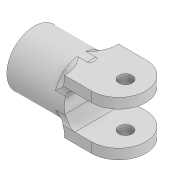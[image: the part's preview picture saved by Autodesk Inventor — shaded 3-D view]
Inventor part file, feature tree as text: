
AUTODESK INVENTOR PART (.ipt)
format: ipt  version: 2022 (Build 260153000, 153)  size: 236,544 bytes
history: native  units: mm
features: extrude x4, sketch x4, fillet x3, projected_geometry x1
ambient origin geometry x8: Origin, YZ Plane, XZ Plane, XY Plane, X Axis, Y Axis, Z Axis, Center Point
bodies: Solid1 (feature_tree)
feature tree (12):
  extrude  "Extrusion1"  Depth=12.2mm
  extrude  "Extrusion2"  Depth=15.0mm TaperAngle=0.0deg
  extrude  "Extrusion3"  Depth=5.0mm
  extrude  "Extrusion4"  Depth=8.0mm
  fillet  "Fillet2"  Radius=8.0mm
  fillet  "Fillet3"  Radius=3.0mm
  fillet  "Fillet4"  Radius=3.0mm
  sketch  "Sketch1"  dims[d0=9.8mm d1=12.2mm]
  sketch  "Sketch2"  dims[d2=2.0mm d3=15.0mm d4=0.0mm]
  projected_geometry  "Projected Loop1"
  sketch  "Sketch3"  dims[d5=2.0mm d6=0.0mm d7=5.0mm]
  sketch  "Sketch4"  dims[d8=5.0mm d9=8.0mm d10=8.0mm d11=3.0mm d12=3.0mm d13=8.0mm d14=8.0mm d15=16.0mm d16=0.0mm d18=4.0mm d19=6.0mm d20=8.0mm d21=16.0mm d22=0.0mm d23=3.0mm d24=3.0mm d25=3.0mm]
